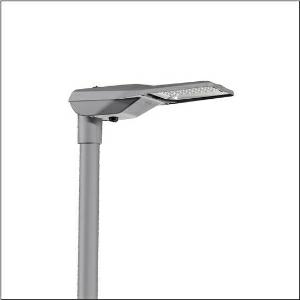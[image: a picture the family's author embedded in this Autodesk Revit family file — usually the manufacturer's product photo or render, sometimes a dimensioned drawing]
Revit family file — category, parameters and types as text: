
# Revit family: streetlight_sl_21_iq_mini___p0_8ab_5xe2r31y08jb_bd99
name_source: partatom
category: Lighting Fixtures
units: mm (PartAtom-declared; Revit-internal decimal feet)

## family parameters
Cut with Voids When Loaded = No
Host = Face
Light Source = No
Part Type = Normal
Room Calculation Point = No
Round Connector Dimension = Use Diameter
Shared = No

## types (1)
- --- (1 x LED, 9740 lm, 72.5 W, 3000K)
    Apparent Load = 73 VA
    CIE Flux Codes = 39 72 97 100 100
    Color Rendering = 70
    Color Temperature = 3000K
    Default Elevation = 1800 mm
    Description = Streetlight SL 21 iQ mini, mast luminaire, primary light control with lens, of PMMA, primary optical cover: cover, of toughened safety glass, transparent, light distribution: P0.8aB, light emission: direct distribution, primary light characteristic: asymmetric, installation type: post-top, side-entry, LED, High Power LED, rated luminous flux: 9.740lm, luminous efficacy: 134lm/W, light colour: 730, colour temperature: 3000K, control gear: iQ-Street Remote, D4i with power reduction, control: pre-setting: logarithmic dimming characteristic, Street-Remote, Auto-Match, Temp-Guard, Lumen-Switch, Night-Set, Smart-Wire, Light-Fading, Desk-Remote (wireless, voltage-free reading and setting of iQ features in the workshop via application-optimized NFC function/RFID function), optimised constant luminous flux control (CLO 2.0), mains connection: 220..240V, AC, 50/60Hz, start of lifetime: 73W, end of service life: 76W, reduction: 33W, luminaire housing, of diecast aluminium, powder-coated, Siteco® metallic grey (DB 702S), corrosivity category C5 mid according to DIN EN ISO 12944, please order mast flange separately, inclination adjustable: 0°, 5°, 10°, 15°, sealing non-destructively replaceable, multi-level sealing system, length: 628mm, width: 235mm, height: 110mm, mast flange for spigot size: 42mm (side-entry): 5XC10008XM4, 60/48mm (side-entry/post-top): 5XC10108XM2, 76/60mm (side-entry/post-top): 5XC10108XM1, mounting height: 4..8m, Smart Interface below and above, protection rating (complete): IP66, insulation class (complete): insulation class II (safety insulation), certification: CE, ENEC, ENEC+, VDE, impact resistance: IK10, permissible operating ambient temperature for outdoor applications: -40..+50°C, standard-compliant lighting for roads and squares, packaging unit: 1 piece

Light Distribution: P0.8aB
    Height = 110 mm
    Lamp = 1 x LED
    Lamp Light Flux = 9740 lm
    Lamp Power = 72.5 W
    Lamp count = 1
    Length = 625 mm
    Luminous efficacy = 134 lm/W
    Manufacturer = Siteco
    ModVariant = No
    Model = 5XE2R31Y08JB
    Number of Poles = 1
    OnlyDefault = Yes
    Power Factor = 1
    Product Name = Streetlight SL 21 iQ mini | P0.8aB
    Product group = mast luminaire | pylon top
    ProductGroupID = 6100
    Protection Class = Protection class II
    Protection Degree = IP 66
    RLX_Detail_Level = 1
    RLX_Emergency_Light_Flux = 0 lm
    RLX_Emergency_Type = 0
    RLX_Emergency_Type_DB = No
    RlxData = <blob elided: 26289 chars, md5=d62a8f74>
    Socket = socket
    Standby Power = 0 W
    System Light Flux = 9740 lm
    System Power = 73 W
    Type Comments = factory setting: luminous flux: 100 % | dim-lin: 254 | 755 mA
    Type Image = l_1003514.jpg
    URL = http://relux.com
    VarID = @adj_071288
    Voltage = 0 V
    Weight = 0.00 kg
    Width = 234 mm

## geometry (parser evidence)
native form markers: Blend x4, Sweep x9
no freeform markers — native parametric forms only
